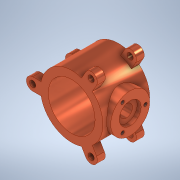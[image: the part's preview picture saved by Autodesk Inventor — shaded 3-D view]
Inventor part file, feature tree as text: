
AUTODESK INVENTOR PART (.ipt)
format: ipt  version: 2021 (Build 250183000, 183)  size: 227,840 bytes
history: native  units: mm
features: extrude x6, sketch x6, other x3, thread x3, pattern_circular x2, mirror x1
ambient origin geometry x8: Origin, YZ Plane, XZ Plane, XY Plane, X Axis, Y Axis, Z Axis, Center Point
bodies: Body1 (feature_tree)
feature tree (21):
  other  "Sólido1"
  extrude  "Extrusão1"  Depth=80.0mm
  extrude  "Extrusão2"  Depth=8.0mm
  pattern_circular  "Padrão circular1"  Count=5  [1 undecoded]
  other  "Plano de trabalho1"
  mirror  "Espelhamento1"
  other  "Plano de trabalho2"
  extrude  "Extrusão3"  Depth=30.0mm TaperAngle=360.0deg
  extrude  "Extrusão4"  Depth=40.0mm
  extrude  "Extrusão5"  Depth=5.0mm TaperAngle=0.0deg
  extrude  "Extrusão6"  Depth=16.0mm
  pattern_circular  "Padrão circular2"  [2 undecoded]
  thread  "Rosca1"  [1 undecoded]
  thread  "Rosca2"  [1 undecoded]
  thread  "Rosca3"  [1 undecoded]
  sketch  "Esboço1"  dims[d0=60.0mm d1=80.0mm]
  sketch  "Esboço2"  dims[d2=60.0mm d3=0.0mm d4=8.0mm]
  sketch  "Esboço3"  dims[d5=16.0mm d6=50.0mm]
  sketch  "Esboço4"  dims[d7=10.0mm d8=0.0mm d9=30.0mm d10=360.0deg]
  sketch  "Esboço5"  dims[d12=30.0mm d13=40.0mm]
  sketch  "Esboço6"  dims[d14=50.0mm d15=5.0mm d16=10.0mm d17=0.0mm d18=0.0mm d19=16.0mm d20=5.0mm d21=0.0mm d22=28.0mm d23=16.0mm d24=5.0mm d25=0.0mm d26=4.5mm d27=10.0mm d28=0.0mm d29=30.0mm d30=360.0deg d32=3.0mm d33=0.0mm d34=3.0mm d35=0.0mm d36=3.0mm d37=0.0mm]
note: 6 required parameter values undecoded (feature->parameter linkage not recoverable at this tier; creation-order binding heuristic only, values carry confidence <= 0.55)
